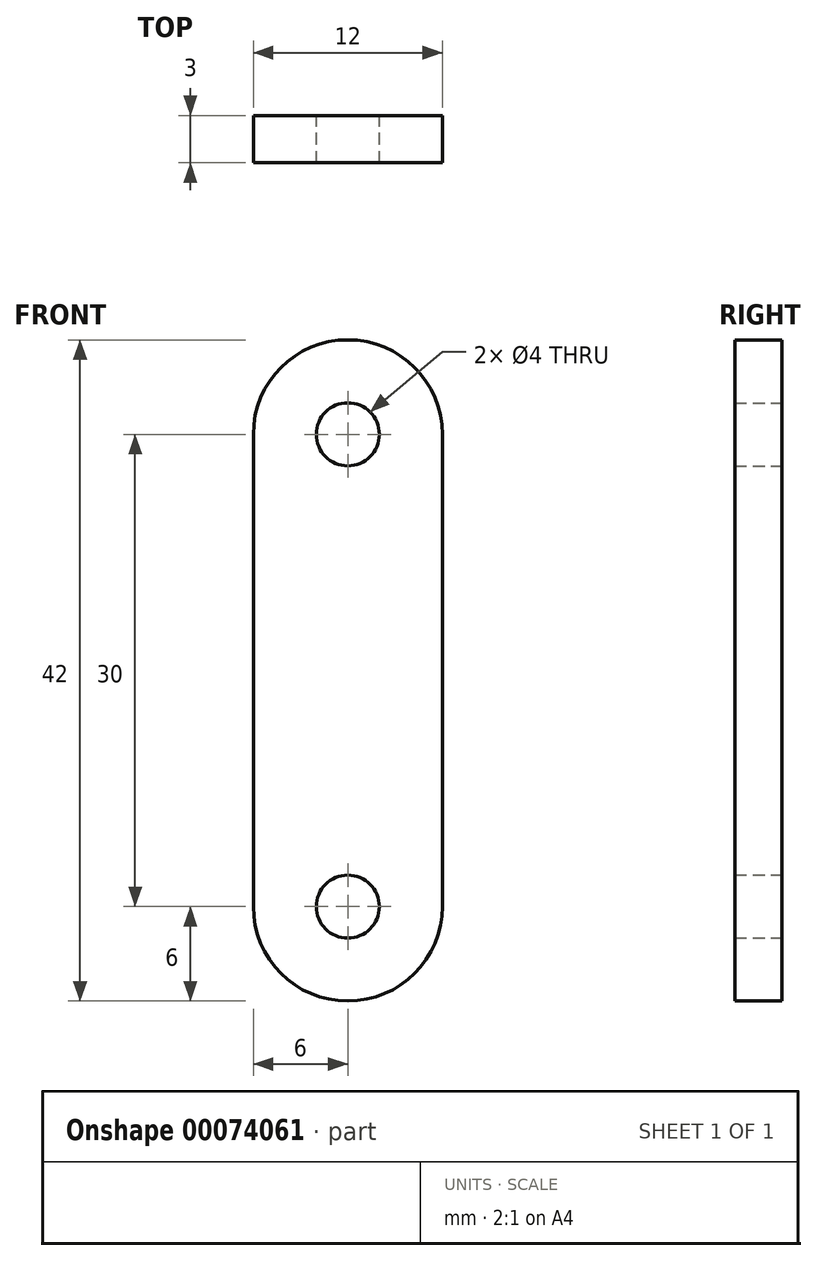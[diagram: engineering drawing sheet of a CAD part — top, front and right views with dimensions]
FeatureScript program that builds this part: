
annotation { "Feature Type Name" : "Feature", "Feature Type Description" : "" }
export const myFeature = defineFeature(function(context is Context, id is Id, definition is map)
    precondition{}
    {
        {
            var Q0;
            Q0=qCreatedBy(makeId("Front.planeOp"),FACE);
            var sketch = newSketch(context, id + "F0", { "sketchPlane" : qUnion([Q0])});
            skCircle(sketch, "E0", {"center": v(0, 0) * mm, "radius": 6 * mm});
            skCircle(sketch, "E1", {"center": v(0, -30) * mm, "radius": 6 * mm});
            skCircle(sketch, "E2", {"center": v(0, 0) * mm, "radius": 2 * mm});
            skCircle(sketch, "E3", {"center": v(0, -30) * mm, "radius": 2 * mm});
            skLineSegment(sketch, "E4", {"start": v(-6, 0) * mm, "end": v(-6, -30) * mm});
            skLineSegment(sketch, "E5", {"start": v(-6, -30) * mm, "end": v(6, -30) * mm});
            skLineSegment(sketch, "E6", {"start": v(6, -30) * mm, "end": v(6, 0) * mm});
            skLineSegment(sketch, "E7", {"start": v(6, 0) * mm, "end": v(-6, 0) * mm});
            skSolve(sketch);
        }
        {
            var Q0;
            Q0=qSketchRegion(id+"F0",true);
            extrude(context, id + "F1", {"entities" : qUnion([Q0]), "depth" : 3 * mm});
        }
    });
